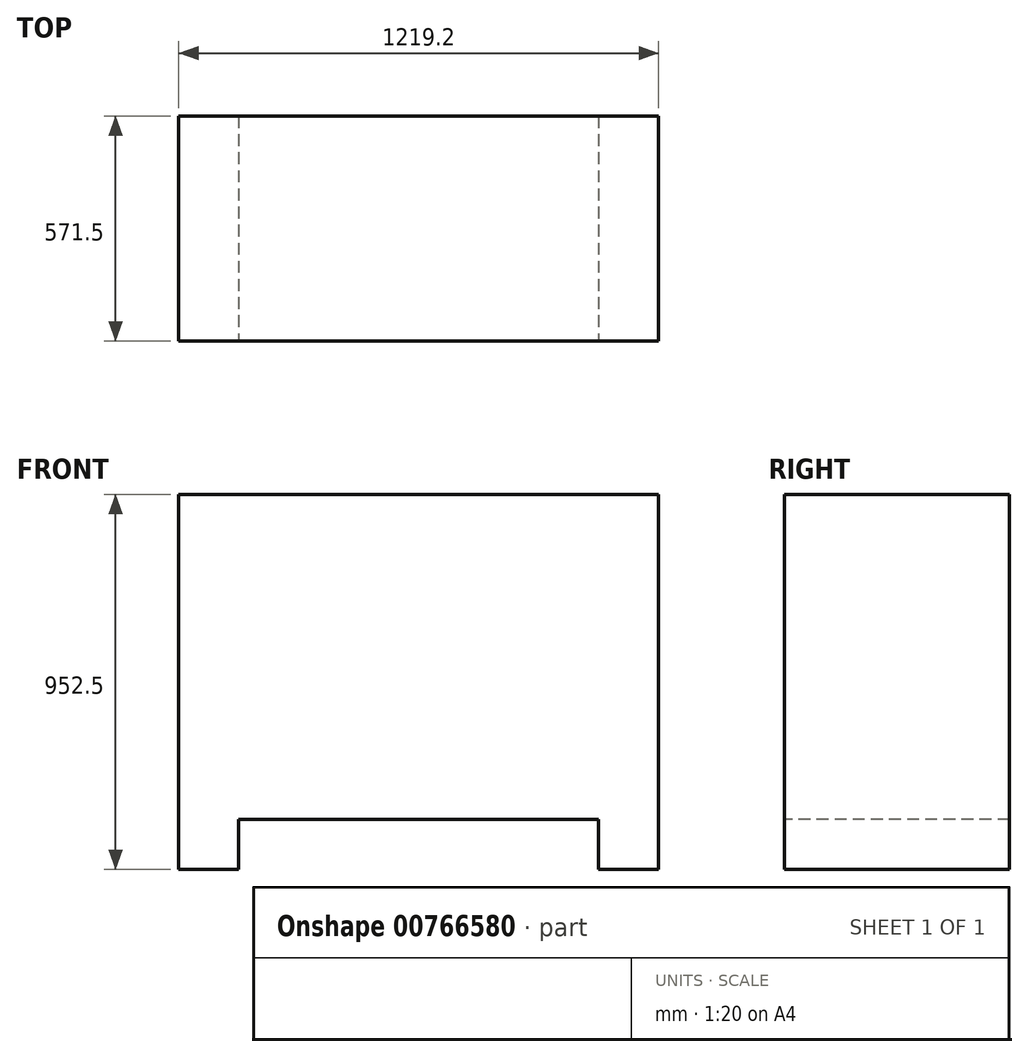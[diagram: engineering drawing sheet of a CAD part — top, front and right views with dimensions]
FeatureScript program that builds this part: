
annotation { "Feature Type Name" : "Feature", "Feature Type Description" : "" }
export const myFeature = defineFeature(function(context is Context, id is Id, definition is map)
    precondition{}
    {
        {
            var Q0;
            Q0=qCreatedBy(makeId("Top.planeOp"),FACE);
            var sketch = newSketch(context, id + "F0", { "sketchPlane" : qUnion([Q0])});
            skLineSegment(sketch, "E0.bottom", {"start": v(-609.6, 285.75) * mm, "end": v(609.6, 285.75) * mm});
            skLineSegment(sketch, "E0.top", {"start": v(-609.6, -285.75) * mm, "end": v(609.6, -285.75) * mm});
            skLineSegment(sketch, "E0.left", {"start": v(-609.6, 285.75) * mm, "end": v(-609.6, -285.75) * mm});
            skLineSegment(sketch, "E0.right", {"start": v(609.6, 285.75) * mm, "end": v(609.6, -285.75) * mm});
            skLineSegment(sketch, "E1", {"start": v(-609.6, 285.75) * mm, "end": v(609.6, -285.75) * mm, "construction": true});
            skSolve(sketch);
        }
        {
            var Q0;
            Q0 = qSketchRegion(id + "F0", true);
            extrude(context, id + "F1", {"entities" : qUnion([Q0]), "depth" : 952.5 * mm, "offsetDistance" : 25.4 * mm});
        }
        {
            var Q0;
            Q0=makeQuery(id+"F1.opExtrude","SWEPT_FACE",FACE,{"disambiguationData":[OSD([sQuery(id+"F0.wireOp",EDGE,"E0.top")])]});
            var sketch = newSketch(context, id + "F2", { "sketchPlane" : qUnion([Q0])});
            skLineSegment(sketch, "E2.bottom", {"start": v(-457.2, 0) * mm, "end": v(457.2, 0) * mm});
            skLineSegment(sketch, "E2.top", {"start": v(-457.2, 127) * mm, "end": v(457.2, 127) * mm});
            skLineSegment(sketch, "E2.left", {"start": v(-457.2, 0) * mm, "end": v(-457.2, 127) * mm});
            skLineSegment(sketch, "E2.right", {"start": v(457.2, 0) * mm, "end": v(457.2, 127) * mm});
            skSolve(sketch);
        }
        {
            var Q0;
            Q0 = qSketchRegion(id + "F2", true);
            extrude(context, id + "F3", {"entities" : qUnion([Q0]), "operationType" : NewBodyOperationType.REMOVE, "endBound" : BoundingType.THROUGH_ALL, "oppositeDirection" : true, "depth" : 25.4 * mm, "offsetDistance" : 25.4 * mm});
        }
    });
